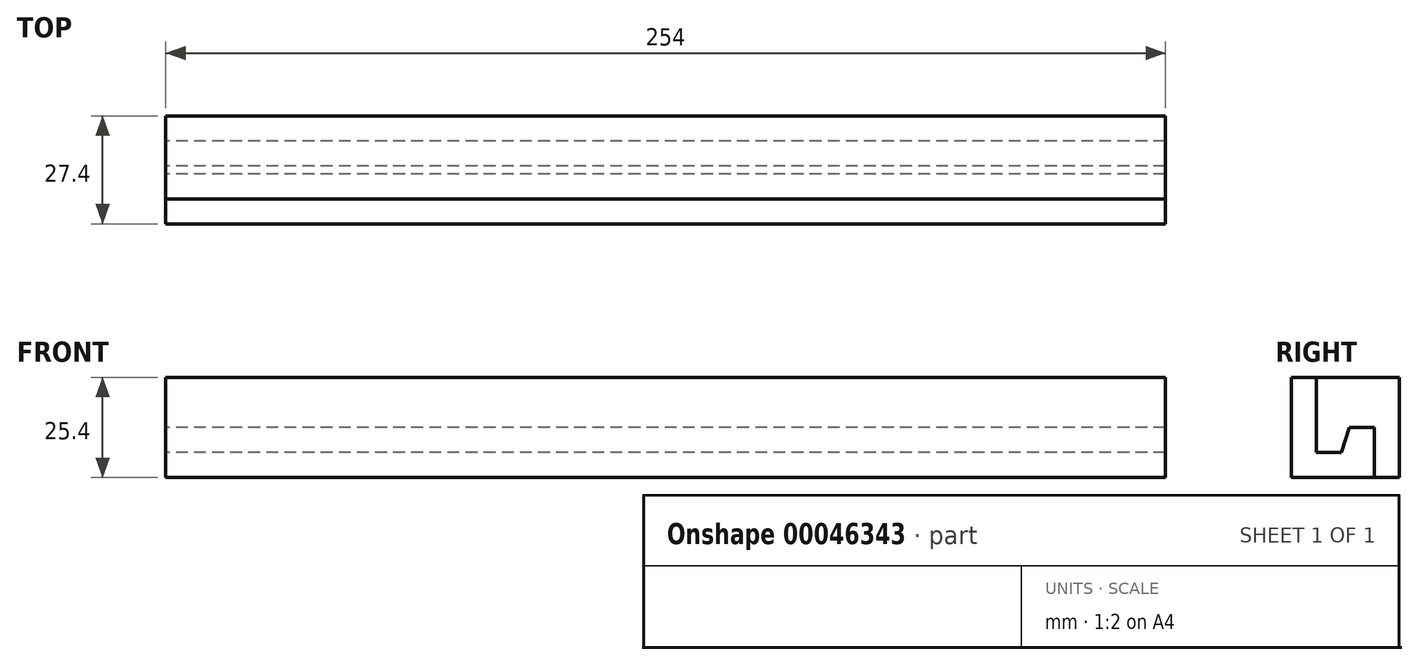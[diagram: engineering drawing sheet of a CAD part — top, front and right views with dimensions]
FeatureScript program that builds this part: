
annotation { "Feature Type Name" : "Feature", "Feature Type Description" : "" }
export const myFeature = defineFeature(function(context is Context, id is Id, definition is map)
    precondition{}
    {
        {
            var Q0;
            Q0=qCreatedBy(makeId("Right.planeOp"),FACE);
            var sketch = newSketch(context, id + "F0", { "sketchPlane" : qUnion([Q0])});
            skLineSegment(sketch, "E0", {"start": v(0, 0) * mm, "end": v(0, 25.4) * mm});
            skLineSegment(sketch, "E1", {"start": v(0, 25.4) * mm, "end": v(6.35, 25.4) * mm});
            skLineSegment(sketch, "E2", {"start": v(6.35, 25.4) * mm, "end": v(6.35, 6.35) * mm});
            skLineSegment(sketch, "E3", {"start": v(6.35, 6.35) * mm, "end": v(12.7, 6.35) * mm});
            skLineSegment(sketch, "E4", {"start": v(12.7, 6.35) * mm, "end": v(14.7, 12.7) * mm});
            skLineSegment(sketch, "E5", {"start": v(14.7, 12.7) * mm, "end": v(21.05, 12.7) * mm});
            skLineSegment(sketch, "E6", {"start": v(21.05, 12.7) * mm, "end": v(21.05, 0) * mm});
            skLineSegment(sketch, "E7", {"start": v(21.05, 0) * mm, "end": v(0, 0) * mm});
            skSolve(sketch);
        }
        {
            var Q0;
            Q0=makeQuery(id+"F0.imprint","IMPRINT",FACE,{"disambiguationData":[TD([[makeQuery(id+"F0.imprint","IMPRINT",EDGE,{"derivedFrom":sQuery(id+"F0.wireOp",EDGE,"E0")}),-1.0]])]});
            extrude(context, id + "F1", {"entities" : qUnion([Q0]), "depth" : 254 * mm});
        }
        {
            var Q0;
            Q0=qCreatedBy(makeId("Right.planeOp"),FACE);
            var sketch = newSketch(context, id + "F2", { "sketchPlane" : qUnion([Q0])});
            skLineSegment(sketch, "E8.0", {"start": v(6.35, 6.35) * mm, "end": v(12.7, 6.35) * mm});
            skLineSegment(sketch, "E8.1", {"start": v(12.7, 6.35) * mm, "end": v(14.7, 12.7) * mm});
            skLineSegment(sketch, "E8.2", {"start": v(14.7, 12.7) * mm, "end": v(21.05, 12.7) * mm});
            skLineSegment(sketch, "E8.3", {"start": v(21.05, 12.7) * mm, "end": v(21.05, 0) * mm});
            skLineSegment(sketch, "E8.4", {"start": v(6.35, 25.4) * mm, "end": v(6.35, 6.35) * mm});
            skLineSegment(sketch, "E9", {"start": v(6.35, 25.4) * mm, "end": v(27.4, 25.4) * mm});
            skLineSegment(sketch, "E10", {"start": v(27.4, 25.4) * mm, "end": v(27.4, 0) * mm});
            skLineSegment(sketch, "E11", {"start": v(27.4, 0) * mm, "end": v(21.05, 0) * mm});
            skSolve(sketch);
        }
        {
            var Q0;
            Q0=makeQuery(id+"F2.imprint","IMPRINT",FACE,{"disambiguationData":[TD([[makeQuery(id+"F2.imprint","IMPRINT",EDGE,{"derivedFrom":sQuery(id+"F2.wireOp",EDGE,"E8.0")}),1.0]])]});
            extrude(context, id + "F3", {"entities" : qUnion([Q0]), "depth" : 254 * mm});
        }
    });
